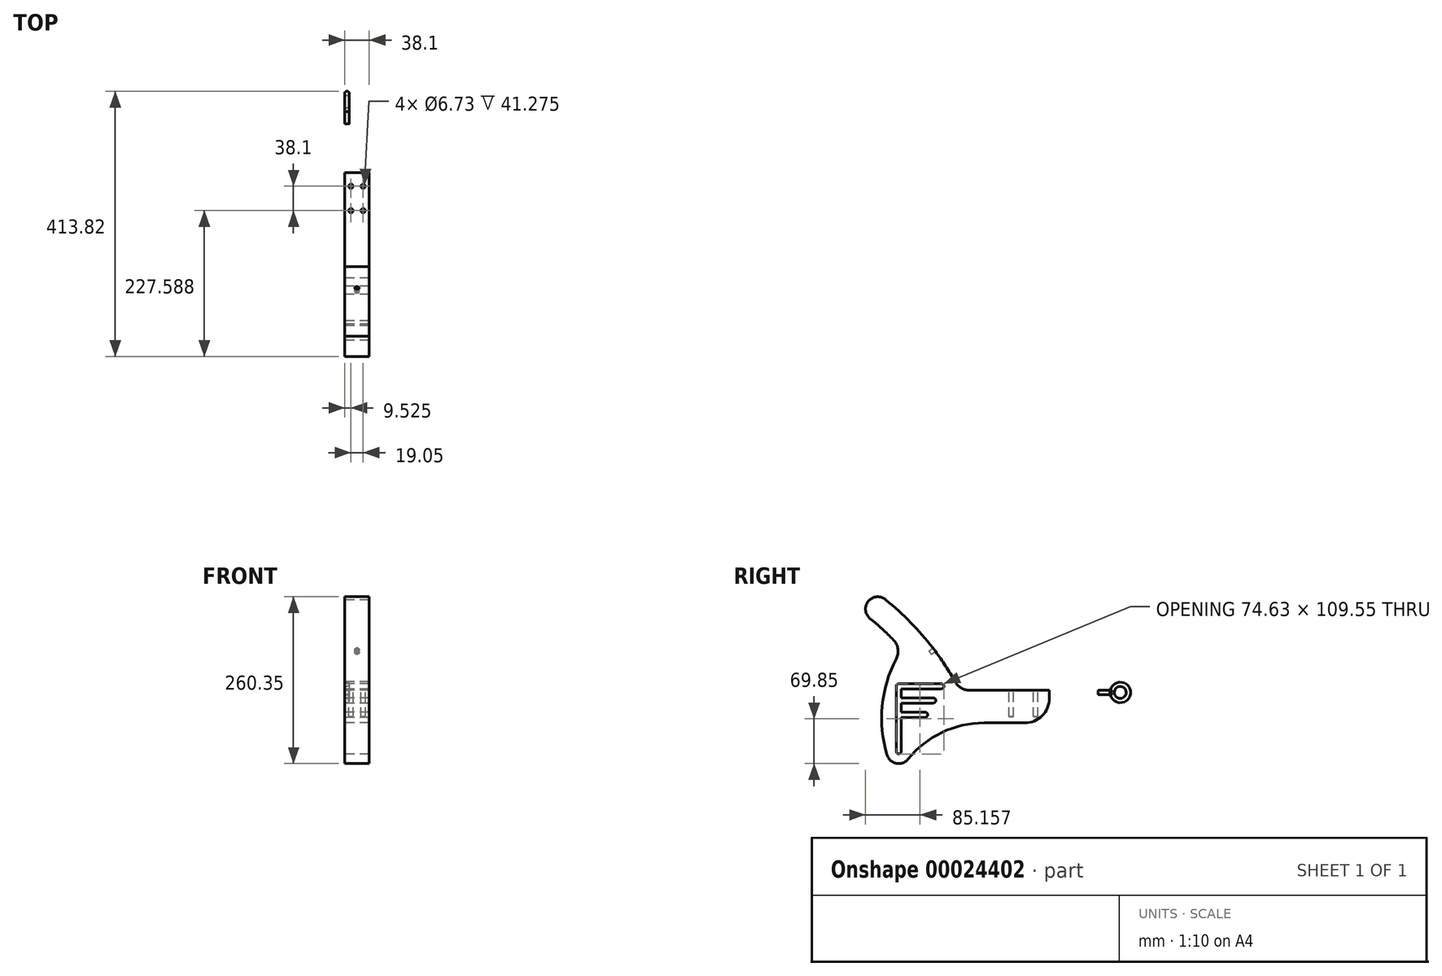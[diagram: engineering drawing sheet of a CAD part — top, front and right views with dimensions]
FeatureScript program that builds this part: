
annotation { "Feature Type Name" : "Feature", "Feature Type Description" : "" }
export const myFeature = defineFeature(function(context is Context, id is Id, definition is map)
    precondition{}
    {
        {
            var Q0;
            Q0=qCreatedBy(makeId("Right.planeOp"),FACE);
            var sketch = newSketch(context, id + "F0", { "sketchPlane" : qUnion([Q0])});
            skLineSegment(sketch, "E0.bottom", {"start": v(-38.1, 0) * mm, "end": v(-101.75, 0) * mm});
            skLineSegment(sketch, "E0.top", {"start": v(0, 50.8) * mm, "end": v(-127, 50.8) * mm});
            skLineSegment(sketch, "E0.left", {"start": v(0, 38.1) * mm, "end": v(0, 50.8) * mm});
            skArc(sketch, "E1", {"start": v(-38.1, 0) * mm, "mid": v(-11.16, 11.16) * mm, "end": v(0, 38.1) * mm});
            skArc(sketch, "E2", {"start": v(-255.05, 192.03) * mm, "mid": v(-282.23, 190.14) * mm, "end": v(-279.71, 163) * mm});
            skArc(sketch, "E3", {"start": v(-146.81, 64.62) * mm, "mid": v(-137.45, 54.53) * mm, "end": v(-124.2, 50.8) * mm});
            skArc(sketch, "E4", {"start": v(-253.18, -49.97) * mm, "mid": v(-238.62, -63.14) * mm, "end": v(-220.15, -56.44) * mm});
            skArc(sketch, "E5", {"start": v(-101.75, 0) * mm, "mid": v(-167.33, -14.83) * mm, "end": v(-220.15, -56.44) * mm});
            skArc(sketch, "E6.trimOffspring", {"start": v(-146.81, 64.62) * mm, "mid": v(-195.06, 133.3) * mm, "end": v(-255.05, 192.03) * mm});
            skArc(sketch, "E7", {"start": v(-238.76, 99.9) * mm, "mid": v(-260.76, 26.39) * mm, "end": v(-253.18, -49.97) * mm});
            skArc(sketch, "E8", {"start": v(-238.76, 99.9) * mm, "mid": v(-236.08, 115.37) * mm, "end": v(-243, 129.46) * mm});
            skArc(sketch, "E9", {"start": v(-238.93, -44.45) * mm, "mid": v(-234.95, -48.43) * mm, "end": v(-230.97, -44.45) * mm});
            skArc(sketch, "E10", {"start": v(-234.95, 61.13) * mm, "mid": v(-237.76, 59.96) * mm, "end": v(-238.93, 57.15) * mm});
            skArc(sketch, "E11", {"start": v(-168.28, 53.17) * mm, "mid": v(-164.3, 57.15) * mm, "end": v(-168.28, 61.13) * mm});
            skArc(sketch, "E12", {"start": v(-180.98, 30.95) * mm, "mid": v(-177, 34.92) * mm, "end": v(-180.98, 38.9) * mm});
            skArc(sketch, "E13", {"start": v(-193.68, 8.72) * mm, "mid": v(-189.7, 12.7) * mm, "end": v(-193.68, 16.68) * mm});
            skLineSegment(sketch, "E14", {"start": v(-234.95, 57.15) * mm, "end": v(-234.95, -44.45) * mm, "construction": true});
            skLineSegment(sketch, "E15", {"start": v(-234.95, 57.15) * mm, "end": v(-168.28, 57.15) * mm, "construction": true});
            skLineSegment(sketch, "E16", {"start": v(-180.97, 34.92) * mm, "end": v(-234.95, 34.92) * mm, "construction": true});
            skLineSegment(sketch, "E17", {"start": v(-193.68, 12.7) * mm, "end": v(-234.95, 12.7) * mm, "construction": true});
            skLineSegment(sketch, "E18", {"start": v(-238.93, 57.15) * mm, "end": v(-238.93, -44.45) * mm});
            skLineSegment(sketch, "E19", {"start": v(-230.97, -44.45) * mm, "end": v(-230.97, 8.72) * mm});
            skLineSegment(sketch, "E20", {"start": v(-168.28, 61.13) * mm, "end": v(-234.95, 61.13) * mm});
            skLineSegment(sketch, "E21", {"start": v(-230.97, 53.17) * mm, "end": v(-168.28, 53.17) * mm});
            skLineSegment(sketch, "E22", {"start": v(-230.97, 38.9) * mm, "end": v(-180.98, 38.9) * mm});
            skLineSegment(sketch, "E23", {"start": v(-230.97, 30.95) * mm, "end": v(-180.98, 30.95) * mm});
            skLineSegment(sketch, "E24", {"start": v(-230.97, 16.68) * mm, "end": v(-193.68, 16.68) * mm});
            skLineSegment(sketch, "E25", {"start": v(-230.97, 8.72) * mm, "end": v(-193.68, 8.72) * mm});
            skLineSegment(sketch, "E26.trimOffspring", {"start": v(-230.97, 38.9) * mm, "end": v(-230.97, 53.17) * mm});
            skLineSegment(sketch, "E27.trimOffspring", {"start": v(-230.97, 16.68) * mm, "end": v(-230.97, 30.95) * mm});
            skArc(sketch, "E28.trimOffspring", {"start": v(-243, 129.46) * mm, "mid": v(-260.86, 146.77) * mm, "end": v(-279.71, 163) * mm});
            skLineSegment(sketch, "E29", {"start": v(-181.78, 116.93) * mm, "end": v(-177.84, 111.75) * mm});
            skSolve(sketch);
        }
        {
            var Q0;
            Q0=makeQuery(id+"F0.imprint","IMPRINT",FACE,{"disambiguationData":[TD([[makeQuery(id+"F0.imprint","IMPRINT",EDGE,{"derivedFrom":sQuery(id+"F0.wireOp",EDGE,"E0.bottom")}),-1.0]])]});
            extrude(context, id + "F1", {"entities" : qUnion([Q0]), "depth" : 38.1 * mm});
        }
        {
            var Q0;
            Q0=makeQuery(id+"F1.opExtrude","SWEPT_FACE",FACE,{"disambiguationData":[OSD([sQuery(id+"F0.wireOp",EDGE,"E0.top")])]});
            var sketch = newSketch(context, id + "F2", { "sketchPlane" : qUnion([Q0])});
            skLineSegment(sketch, "E30", {"start": v(19.05, 0) * mm, "end": v(19.05, -21.08) * mm, "construction": true});
            skLineSegment(sketch, "E31", {"start": v(19.05, -21.08) * mm, "end": v(19.05, -59.18) * mm, "construction": true});
            skCircle(sketch, "E32", {"center": v(9.53, -59.18) * mm, "radius": 3.37 * mm});
            skLineSegment(sketch, "E33", {"start": v(38.1, -59.18) * mm, "end": v(0, -59.18) * mm, "construction": true});
            skLineSegment(sketch, "E34", {"start": v(38.1, -21.08) * mm, "end": v(0, -21.08) * mm, "construction": true});
            skCircle(sketch, "E35", {"center": v(28.58, -59.18) * mm, "radius": 3.37 * mm});
            skCircle(sketch, "E36", {"center": v(28.58, -21.08) * mm, "radius": 3.37 * mm});
            skCircle(sketch, "E37", {"center": v(9.53, -21.08) * mm, "radius": 3.37 * mm});
            skSolve(sketch);
        }
        {
            var Q0;
            Q0=makeQuery(id+"F2.imprint","IMPRINT",FACE,{"disambiguationData":[TD([[makeQuery(id+"F2.imprint","IMPRINT",EDGE,{"derivedFrom":sQuery(id+"F2.wireOp",EDGE,"E37")}),1.0]])]});
            var Q1;
            Q1=makeQuery(id+"F2.imprint","IMPRINT",FACE,{"disambiguationData":[TD([[makeQuery(id+"F2.imprint","IMPRINT",EDGE,{"derivedFrom":sQuery(id+"F2.wireOp",EDGE,"E36")}),1.0]])]});
            var Q2;
            Q2=makeQuery(id+"F2.imprint","IMPRINT",FACE,{"disambiguationData":[TD([[makeQuery(id+"F2.imprint","IMPRINT",EDGE,{"derivedFrom":sQuery(id+"F2.wireOp",EDGE,"E35")}),1.0]])]});
            var Q3;
            Q3=makeQuery(id+"F2.imprint","IMPRINT",FACE,{"disambiguationData":[TD([[makeQuery(id+"F2.imprint","IMPRINT",EDGE,{"derivedFrom":sQuery(id+"F2.wireOp",EDGE,"E32")}),1.0]])]});
            extrude(context, id + "F3", {"entities" : qUnion([Q0, Q1, Q2, Q3]), "operationType" : NewBodyOperationType.REMOVE, "oppositeDirection" : true, "depth" : 41.27 * mm});
        }
        {
            var Q0;
            Q0=qCreatedBy(makeId("Right.planeOp"),FACE);
            var sketch = newSketch(context, id + "F4", { "sketchPlane" : qUnion([Q0])});
            skLineSegment(sketch, "E38.bottom", {"start": v(76.05, 50.93) * mm, "end": v(95.3, 50.93) * mm});
            skLineSegment(sketch, "E38.top", {"start": v(76.05, 44.2) * mm, "end": v(95.3, 44.2) * mm});
            skLineSegment(sketch, "E38.left", {"start": v(76.05, 50.93) * mm, "end": v(76.05, 44.2) * mm});
            skLineSegment(sketch, "E38.right", {"start": v(111, 50.93) * mm, "end": v(111, 44.2) * mm, "construction": true});
            skCircle(sketch, "E39", {"center": v(111, 47.56) * mm, "radius": 16.06 * mm});
            skCircle(sketch, "E40", {"center": v(111, 47.56) * mm, "radius": 9.33 * mm});
            skLineSegment(sketch, "E41", {"start": v(95.3, 50.93) * mm, "end": v(111, 50.93) * mm, "construction": true});
            skLineSegment(sketch, "E42", {"start": v(95.3, 44.2) * mm, "end": v(111, 44.2) * mm, "construction": true});
            skSolve(sketch);
        }
        {
            var Q0;
            Q0=makeQuery(id+"F4.imprint","IMPRINT",FACE,{"disambiguationData":[TD([[makeQuery(id+"F4.imprint","IMPRINT",EDGE,{"derivedFrom":sQuery(id+"F4.wireOp",EDGE,"E40")}),-1.0]])]});
            var Q1;
            {var subQ2=sQuery(id+"F4.wireOp",EDGE,"E38.bottom");Q1=makeQuery(id+"F4.imprint","IMPRINT",FACE,{"disambiguationData":[TD([[makeQuery(id+"F4.imprint","IMPRINT",EDGE,{"derivedFrom":subQ2}),-1.0]])]});}
            var Q2;
            Q2=sQuery(id+"F4.wireOp",EDGE,"E42");
            var Q3;
            Q3=sQuery(id+"F4.wireOp",EDGE,"E40");
            extrude(context, id + "F5", {"entities" : qUnion([Q0, Q1]), "surfaceEntities" : qUnion([Q2, Q3]), "depth" : 6.73 * mm});
        }
        {
            var Q0;
            Q0=makeQuery(id+"F5.opExtrude","CAP_EDGE",EDGE,{"disambiguationData":[OSD([sQuery(id+"F4.wireOp",EDGE,"E38.bottom")])],"isStart":false});
            var Q1;
            Q1=makeQuery(id+"F5.opExtrude","CAP_EDGE",EDGE,{"disambiguationData":[OSD([sQuery(id+"F4.wireOp",EDGE,"E38.top")])],"isStart":false});
            var Q2;
            Q2=makeQuery(id+"F5.opExtrude","CAP_EDGE",EDGE,{"disambiguationData":[OSD([sQuery(id+"F4.wireOp",EDGE,"E38.top")])],"isStart":true});
            var Q3;
            Q3=makeQuery(id+"F5.opExtrude","CAP_EDGE",EDGE,{"disambiguationData":[OSD([sQuery(id+"F4.wireOp",EDGE,"E38.bottom")])],"isStart":true});
            var Q4;
            Q4=makeQuery(id+"F5.opExtrude","CAP_EDGE",EDGE,{"disambiguationData":[OSD([sQuery(id+"F4.wireOp",EDGE,"E40")])],"isStart":false});
            var Q5;
            Q5=makeQuery(id+"F5.opExtrude","CAP_EDGE",EDGE,{"disambiguationData":[OSD([sQuery(id+"F4.wireOp",EDGE,"E40")])],"isStart":true});
            fillet(context, id + "F6", {"entities" : qUnion([Q0, Q1, Q2, Q3, Q4, Q5]), "radius" : 3.37 * mm, "tangentPropagation" : true, "allowEdgeOverflow" : false});
        }
        {
            var Q0;
            Q0=makeQuery(id+"F5.opExtrude","CAP_EDGE",EDGE,{"disambiguationData":[OSD([sQuery(id+"F4.wireOp",EDGE,"E39")])],"isStart":false});
            var Q1;
            Q1=makeQuery(id+"F5.opExtrude","CAP_EDGE",EDGE,{"disambiguationData":[OSD([sQuery(id+"F4.wireOp",EDGE,"E39")])],"isStart":true});
            fillet(context, id + "F7", {"entities" : qUnion([Q0, Q1]), "radius" : 3.05 * mm, "tangentPropagation" : true, "rho" : 0.5, "crossSection" : FilletCrossSection.CONIC, "allowEdgeOverflow" : false});
        }
        {
            var Q0;
            Q0=makeQuery(id+"F1.opExtrude","SWEPT_FACE",FACE,{"disambiguationData":[OSD([sQuery(id+"F0.wireOp",EDGE,"E29")])]});
            var sketch = newSketch(context, id + "F8", { "sketchPlane" : qUnion([Q0])});
            skLineSegment(sketch, "E43", {"start": v(-38.1, 199.92) * mm, "end": v(0, 199.92) * mm, "construction": true});
            skCircle(sketch, "E44", {"center": v(-19.05, 199.92) * mm, "radius": 3.37 * mm});
            skSolve(sketch);
        }
        {
            var Q0;
            {var subQ0=sQuery(id+"F0.wireOp",EDGE,"E6.trimOffspring");var subQ1=sQuery(id+"F0.wireOp",EDGE,"E29");var subQ3=sQuery(id+"F8.wireOp",EDGE,"E44");var subQ6=makeQuery(id+"F1.opExtrude","SWEPT_EDGE",EDGE,{"disambiguationData":[OSD([subQ0,subQ1]),TDD([makeQuery(id+"F0.imprint","INTERSECT",VERTEX,{"disambiguationData":[OD(0.0)],"derivedFrom":[subQ0,subQ1]})])]});var subQ8=makeQuery(id+"F8.imprint","INTERSECT",VERTEX,{"disambiguationData":[OD(0.0)],"derivedFrom":[subQ6,subQ3]});Q0=makeQuery(id+"F8.imprint","IMPRINT",FACE,{"disambiguationData":[TD([[makeQuery(id+"F8.imprint","IMPRINT",EDGE,{"disambiguationData":[TD([[subQ8,-1.0]])],"derivedFrom":subQ3}),1.0]])]});}
            var Q1;
            Q1=sQuery(id+"F8.wireOp",EDGE,"E44");
            extrude(context, id + "F9", {"entities" : qUnion([Q0]), "operationType" : NewBodyOperationType.REMOVE, "surfaceEntities" : qUnion([Q1]), "oppositeDirection" : true, "depth" : 7.62 * mm});
        }
    });
